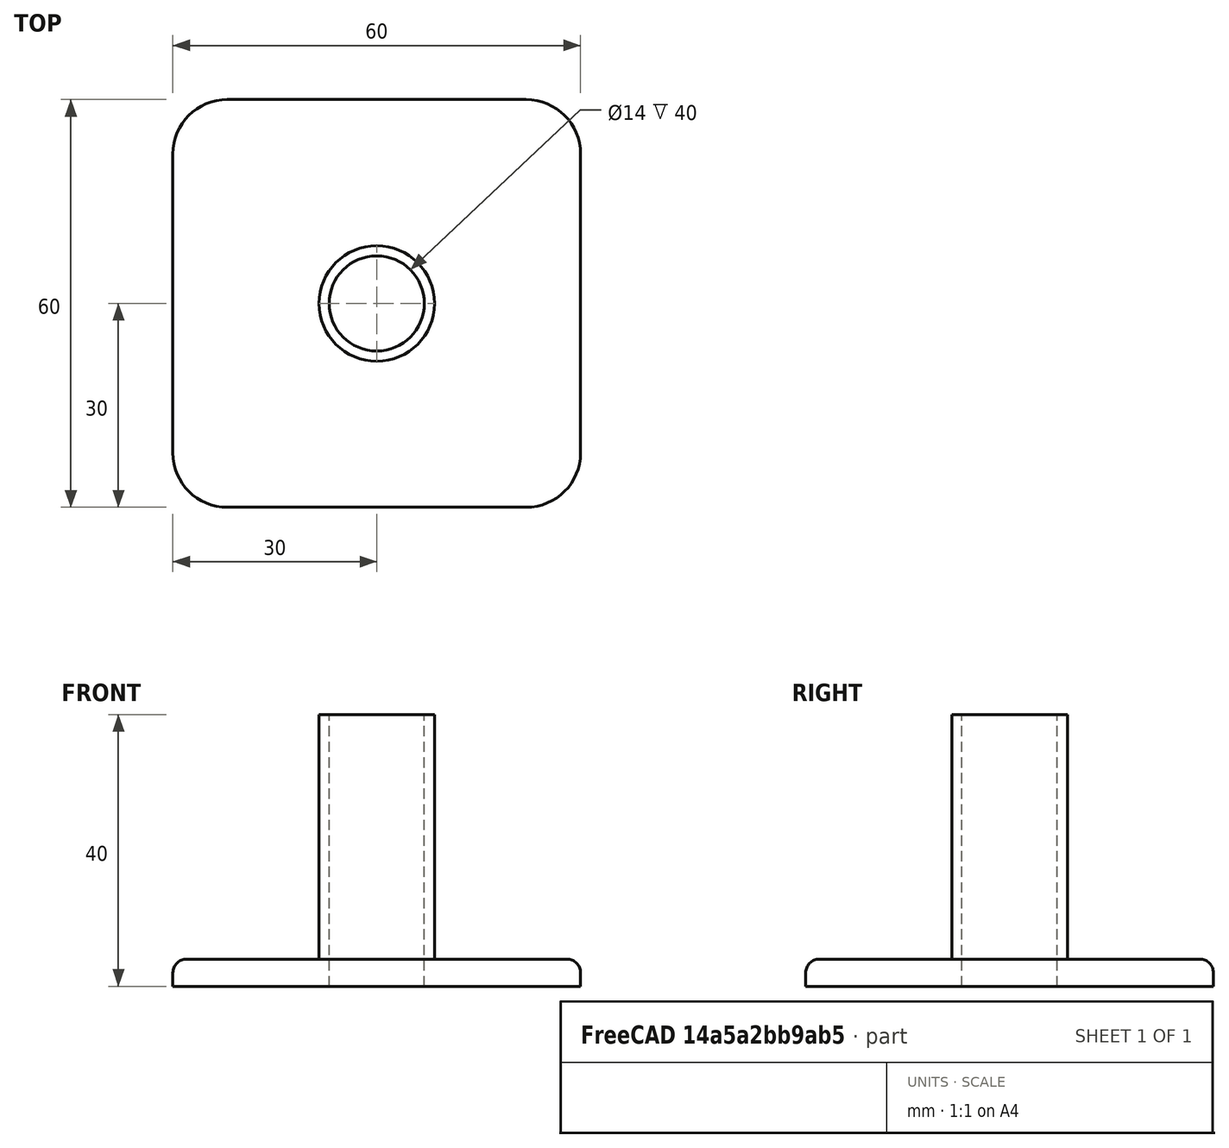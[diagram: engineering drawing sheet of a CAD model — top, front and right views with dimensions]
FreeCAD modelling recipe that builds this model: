
FCSTD DOCUMENT  (FreeCAD 0.16R6706 (Git))
Label: Rocket_stand
License: All rights reserved
LicenseURL: http://en.wikipedia.org/wiki/All_rights_reserved
objects: Part::Cylinder×2, Part::Fillet×2, Part::Box×1, Part::MultiFuse×1, Part::Cut×1
note: 7 computed .brp shape members not serialized (recipe doc carries the construction recipe); baked Part::Feature solids carry a one-line shape summary decoded from their .brp

FEATURE [Part::Cylinder] Cylinder
  Angle = 360
  Height = 40
  Radius = 8.5
FEATURE [Part::Cylinder] Cylinder001
  Angle = 360
  Height = 50
  Radius = 7
FEATURE [Part::Box] Box  label="Cube"
  Height = 4
  Length = 60
  Placement = pos=(-30,-30,0) rot=(0,0,1;0rad)
  Width = 60
FEATURE [Part::Fillet] Fillet
  Base = -> Box
  Edges = 4 edges r=8: [Edge1,Edge3,Edge5,Edge7]
FEATURE [Part::Fillet] Fillet001
  Base = -> Fillet
  Edges = 8 edges r=2: [Edge1,Edge5,Edge6,Edge7,Edge8,Edge9,Edge10,Edge11]
FEATURE [Part::MultiFuse] Fusion
  Shapes = -> [Fillet001,Cylinder]
FEATURE [Part::Cut] Cut
  Base = -> Fusion
  Tool = -> Cylinder001
